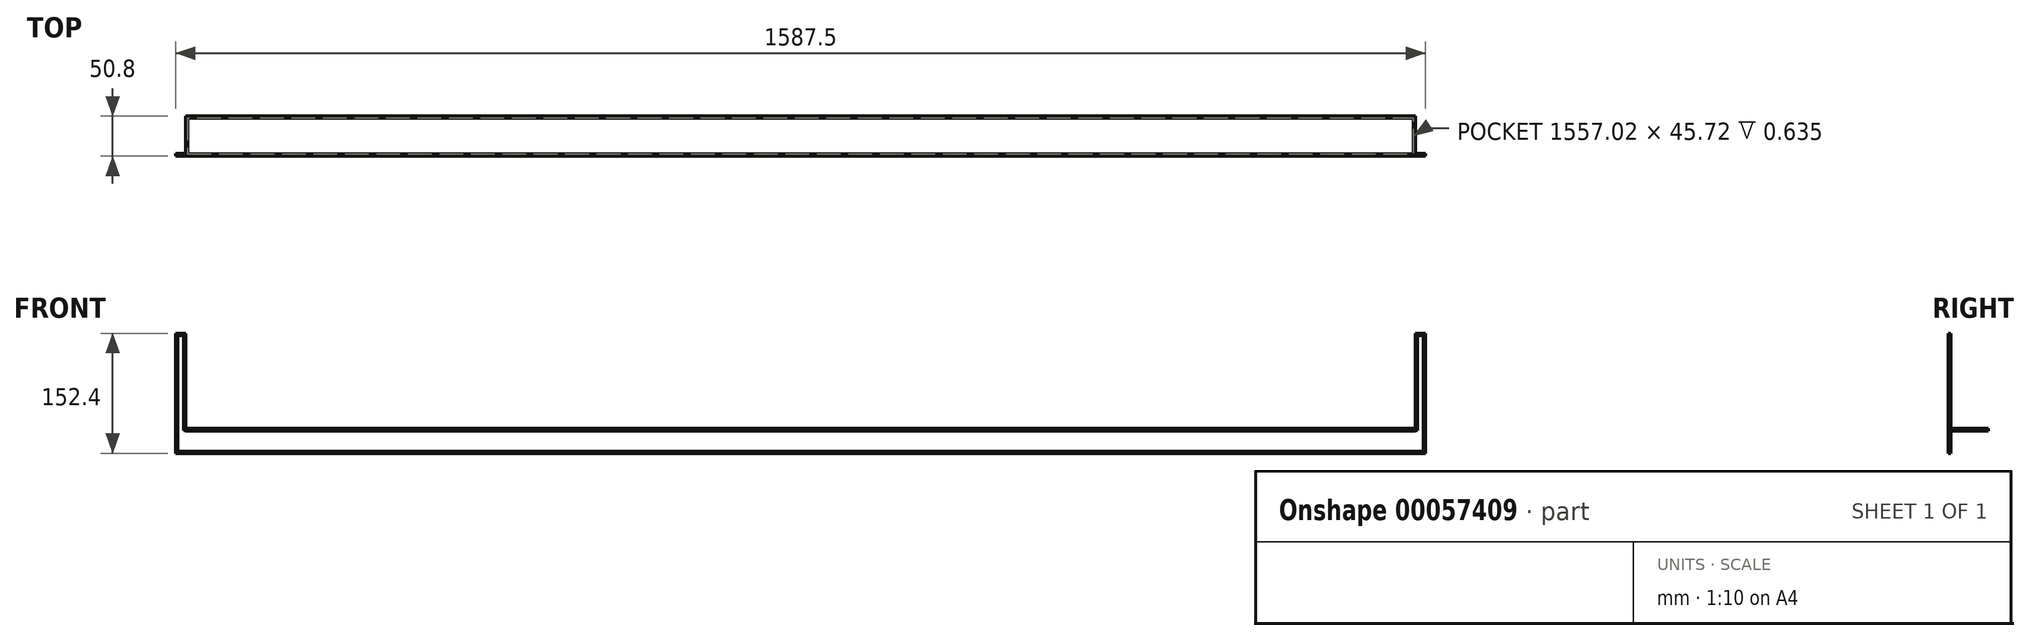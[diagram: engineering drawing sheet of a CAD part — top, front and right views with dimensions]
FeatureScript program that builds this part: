
annotation { "Feature Type Name" : "Feature", "Feature Type Description" : "" }
export const myFeature = defineFeature(function(context is Context, id is Id, definition is map)
    precondition{}
    {
        {
            var Q0;
            Q0=qCreatedBy(makeId("Front.planeOp"),FACE);
            var sketch = newSketch(context, id + "F0", { "sketchPlane" : qUnion([Q0])});
            skLineSegment(sketch, "E0", {"start": v(0, -65.84) * mm, "end": v(0, 66.55) * mm, "construction": true});
            skLineSegment(sketch, "E1", {"start": v(-66.38, 0) * mm, "end": v(67.39, 0) * mm, "construction": true});
            skLineSegment(sketch, "E2", {"start": v(-793.75, 156.19) * mm, "end": v(-781.05, 156.19) * mm});
            skLineSegment(sketch, "E3", {"start": v(-781.05, 156.19) * mm, "end": v(-781.05, 35.54) * mm});
            skLineSegment(sketch, "E4", {"start": v(-781.05, 35.54) * mm, "end": v(781.05, 35.54) * mm});
            skLineSegment(sketch, "E5", {"start": v(781.05, 35.54) * mm, "end": v(781.05, 156.19) * mm});
            skLineSegment(sketch, "E6", {"start": v(781.05, 156.19) * mm, "end": v(793.75, 156.19) * mm});
            skLineSegment(sketch, "E7", {"start": v(793.75, 156.19) * mm, "end": v(793.75, 3.79) * mm});
            skLineSegment(sketch, "E8", {"start": v(793.75, 3.79) * mm, "end": v(-793.75, 3.79) * mm});
            skLineSegment(sketch, "E9", {"start": v(-793.75, 3.79) * mm, "end": v(-793.75, 156.19) * mm});
            skSolve(sketch);
        }
        {
            var Q0;
            Q0=makeQuery(id+"F0.imprint","IMPRINT",FACE,{"disambiguationData":[TD([[makeQuery(id+"F0.imprint","IMPRINT",EDGE,{"derivedFrom":sQuery(id+"F0.wireOp",EDGE,"E2")}),-1.0]])]});
            extrude(context, id + "F1", {"entities" : qUnion([Q0]), "depth" : 3.17 * mm});
        }
        {
            var Q0;
            Q0=makeQuery(id+"F1.opExtrude","CAP_EDGE",EDGE,{"disambiguationData":[OSD([sQuery(id+"F0.wireOp",EDGE,"E4")])],"isStart":false});
            cPlane(context, id + "F2", {"entities" : qUnion([Q0]), "cplaneType" : CPlaneType.LINE_ANGLE, "offset" : 152.4 * mm, "angle" : 90 * degree, "width" : 152.4 * mm, "height" : 152.4 * mm});
        }
        {
            var Q0;
            Q0=qCreatedBy(id+"F2.planeOp",FACE);
            var sketch = newSketch(context, id + "F3", { "sketchPlane" : qUnion([Q0])});
            skLineSegment(sketch, "E10.0", {"start": v(-781.05, -3.18) * mm, "end": v(781.05, -3.18) * mm});
            skLineSegment(sketch, "E11.top", {"start": v(-781.05, 47.63) * mm, "end": v(781.05, 47.63) * mm});
            skLineSegment(sketch, "E11.left", {"start": v(-781.05, -3.18) * mm, "end": v(-781.05, 47.63) * mm});
            skLineSegment(sketch, "E11.right", {"start": v(781.05, -3.18) * mm, "end": v(781.05, 47.63) * mm});
            skSolve(sketch);
        }
        {
            var Q0;
            Q0=makeQuery(id+"F3.imprint","IMPRINT",FACE,{"disambiguationData":[TD([[makeQuery(id+"F3.imprint","IMPRINT",EDGE,{"derivedFrom":sQuery(id+"F3.wireOp",EDGE,"E10.0")}),1.0]])]});
            extrude(context, id + "F4", {"entities" : qUnion([Q0]), "operationType" : NewBodyOperationType.ADD, "oppositeDirection" : true, "depth" : 3.17 * mm});
        }
        {
            var Q0;
            Q0=makeQuery(id+"F4.boolean.opBoolean","MERGE",FACE,{"derivedFrom":[makeQuery(id+"F1.opExtrude","SWEPT_FACE",FACE,{"disambiguationData":[OSD([sQuery(id+"F0.wireOp",EDGE,"E4")])]}),makeQuery(id+"F4.opExtrude","CAP_FACE",FACE,{"disambiguationData":[OSD([sQuery(id+"F3.wireOp",EDGE,"E10.0"),sQuery(id+"F3.wireOp",EDGE,"E11.top"),sQuery(id+"F3.wireOp",EDGE,"E11.left"),sQuery(id+"F3.wireOp",EDGE,"E11.right")])],"isStart":true})]});
            shell(context, id + "F5", {"entities" : qUnion([Q0]), "thickness" : 2.54 * mm});
        }
        {
            var Q0;
            Q0=makeQuery(id+"F1.opExtrude","CAP_FACE",FACE,{"disambiguationData":[OSD([sQuery(id+"F0.wireOp",EDGE,"E2"),sQuery(id+"F0.wireOp",EDGE,"E3"),sQuery(id+"F0.wireOp",EDGE,"E4"),sQuery(id+"F0.wireOp",EDGE,"E5"),sQuery(id+"F0.wireOp",EDGE,"E6"),sQuery(id+"F0.wireOp",EDGE,"E7"),sQuery(id+"F0.wireOp",EDGE,"E8"),sQuery(id+"F0.wireOp",EDGE,"E9")])],"isStart":false});
            shell(context, id + "F6", {"entities" : qUnion([Q0]), "thickness" : 2.54 * mm});
        }
    });
